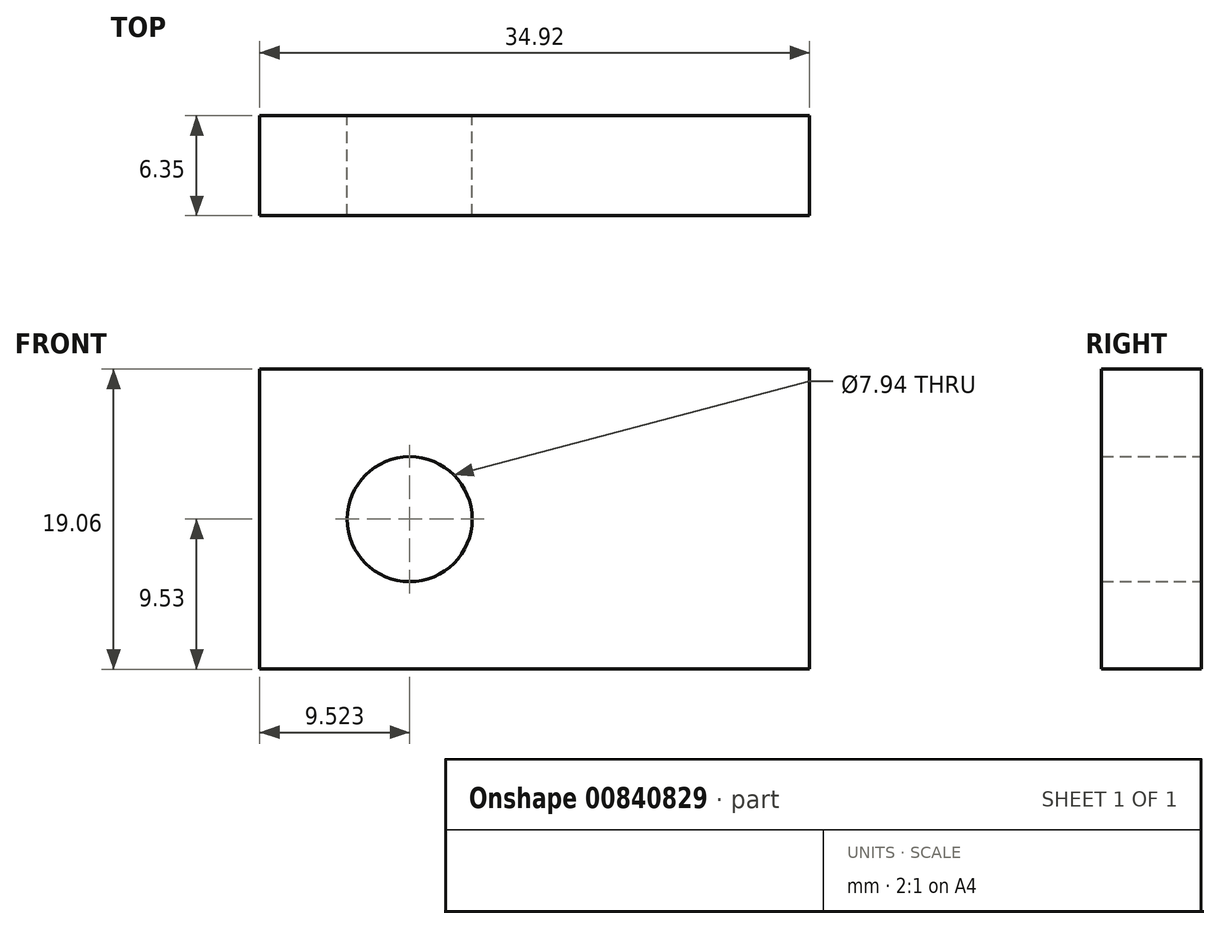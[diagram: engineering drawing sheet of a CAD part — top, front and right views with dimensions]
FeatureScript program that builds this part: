
annotation { "Feature Type Name" : "Feature", "Feature Type Description" : "" }
export const myFeature = defineFeature(function(context is Context, id is Id, definition is map)
    precondition{}
    {
        {
            var Q0;
            Q0=qCreatedBy(makeId("Front.planeOp"),FACE);
            var sketch = newSketch(context, id + "F0", { "sketchPlane" : qUnion([Q0])});
            skLineSegment(sketch, "E0.bottom", {"start": v(17.46, 9.53) * mm, "end": v(-17.46, 9.53) * mm});
            skLineSegment(sketch, "E0.top", {"start": v(17.46, -9.53) * mm, "end": v(-17.46, -9.53) * mm});
            skLineSegment(sketch, "E0.left", {"start": v(17.46, 9.53) * mm, "end": v(17.46, -9.53) * mm});
            skLineSegment(sketch, "E0.right", {"start": v(-17.46, 9.53) * mm, "end": v(-17.46, -9.53) * mm});
            skPoint(sketch, "E0.middle", {"position": v(0, 0) * mm});
            skCircle(sketch, "E1", {"center": v(-7.94, 0) * mm, "radius": 3.97 * mm});
            skSolve(sketch);
        }
        {
            var Q0;
            Q0 = qSketchRegion(id + "F0", true);
            extrude(context, id + "F1", {"entities" : qUnion([Q0]), "depth" : 6.35 * mm, "offsetDistance" : 25.4 * mm});
        }
    });
